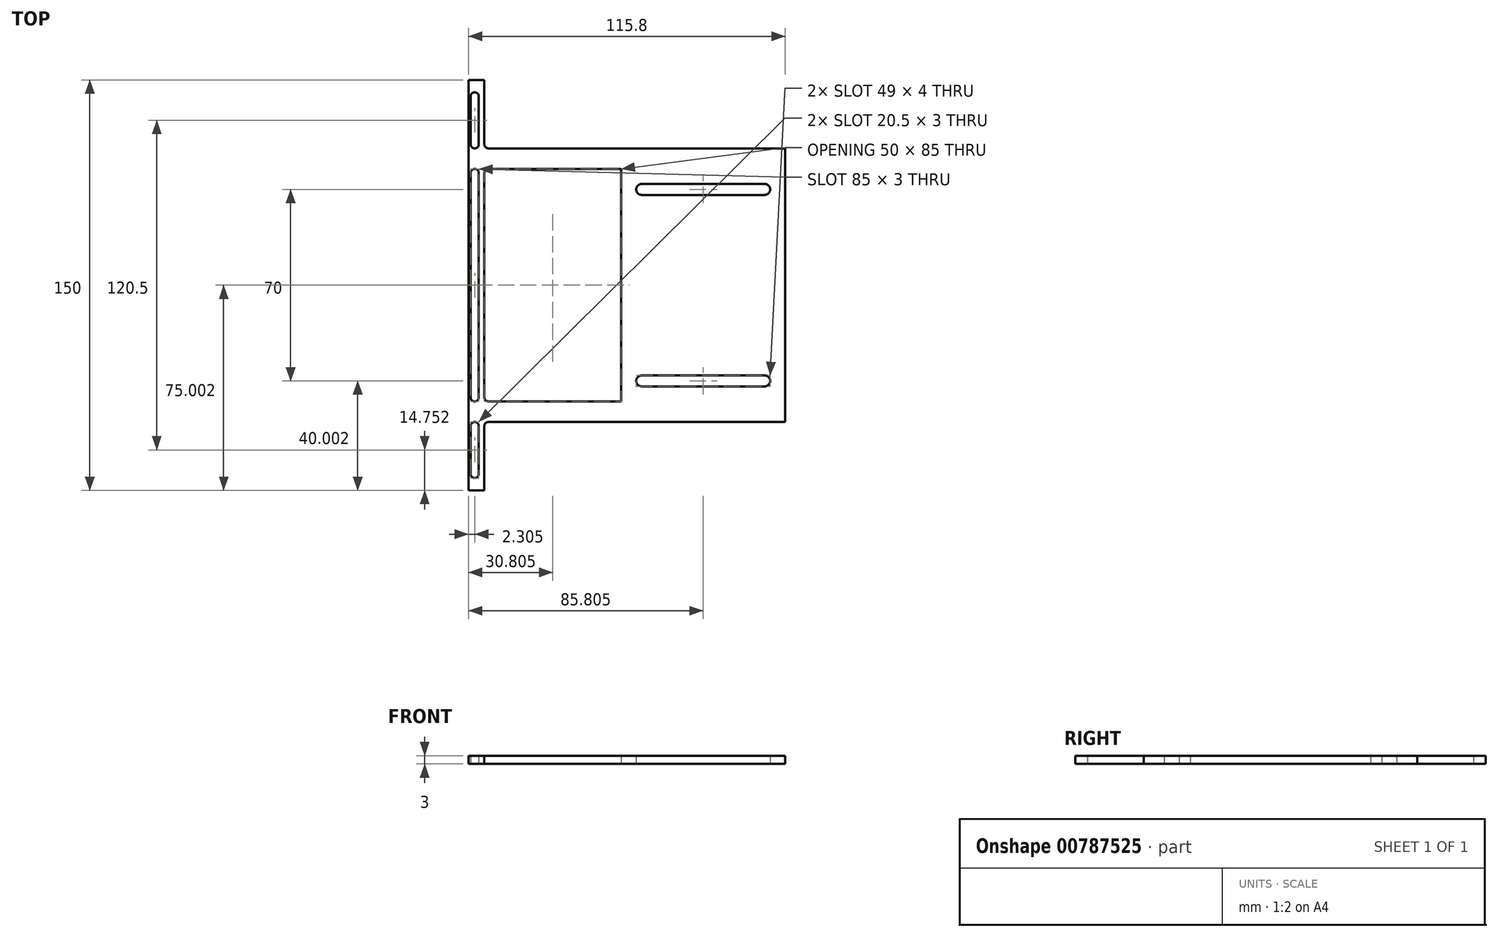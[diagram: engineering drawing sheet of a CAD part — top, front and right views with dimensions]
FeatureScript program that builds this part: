
annotation { "Feature Type Name" : "Feature", "Feature Type Description" : "" }
export const myFeature = defineFeature(function(context is Context, id is Id, definition is map)
    precondition{}
    {
        {
            var Q0;
            Q0=qCreatedBy(makeId("Top.planeOp"),FACE);
            var sketch = newSketch(context, id + "F0", { "sketchPlane" : qUnion([Q0])});
            skLineSegment(sketch, "E0.bottom", {"start": v(-8.05, 60.1) * mm, "end": v(-116.55, 60.1) * mm});
            skLineSegment(sketch, "E0.top", {"start": v(-8.05, -39.9) * mm, "end": v(-116.55, -39.9) * mm});
            skLineSegment(sketch, "E0.left", {"start": v(-8.05, 60.1) * mm, "end": v(-8.05, -39.9) * mm});
            skLineSegment(sketch, "E0.right", {"start": v(-118.05, 51.1) * mm, "end": v(-118.05, -30.9) * mm});
            skLineSegment(sketch, "E1.bottom", {"start": v(-116.55, 52.6) * mm, "end": v(-68.05, 52.6) * mm});
            skLineSegment(sketch, "E1.top", {"start": v(-116.55, -32.4) * mm, "end": v(-68.05, -32.4) * mm});
            skLineSegment(sketch, "E1.right", {"start": v(-68.05, 52.6) * mm, "end": v(-68.05, -32.4) * mm});
            skLineSegment(sketch, "E2.bottom", {"start": v(-118.05, 85.1) * mm, "end": v(-123.85, 85.1) * mm});
            skLineSegment(sketch, "E2.top", {"start": v(-118.05, -64.9) * mm, "end": v(-123.85, -64.9) * mm});
            skLineSegment(sketch, "E2.left", {"start": v(-118.05, 85.1) * mm, "end": v(-118.05, 61.6) * mm});
            skLineSegment(sketch, "E2.right", {"start": v(-123.85, 85.1) * mm, "end": v(-123.85, -64.9) * mm});
            skLineSegment(sketch, "E3.trimOffspring", {"start": v(-118.05, -41.4) * mm, "end": v(-118.05, -64.9) * mm});
            skLineSegment(sketch, "E4.trimOffspring", {"start": v(-118.05, 52.6) * mm, "end": v(-118.05, -32.4) * mm});
            skArc(sketch, "E5", {"start": v(-15.55, 43.1) * mm, "mid": v(-13.55, 45.1) * mm, "end": v(-15.55, 47.1) * mm});
            skArc(sketch, "E6", {"start": v(-60.55, 47.1) * mm, "mid": v(-62.55, 45.1) * mm, "end": v(-60.55, 43.1) * mm});
            skLineSegment(sketch, "E7", {"start": v(-60.55, 47.1) * mm, "end": v(-15.55, 47.1) * mm});
            skLineSegment(sketch, "E8", {"start": v(-60.55, 43.1) * mm, "end": v(-15.55, 43.1) * mm});
            skLineSegment(sketch, "E9", {"start": v(-8.05, 10.1) * mm, "end": v(-21.34, 10.1) * mm, "construction": true});
            skArc(sketch, "E10.MirrorCS", {"start": v(-60.55, -26.9) * mm, "mid": v(-62.55, -24.9) * mm, "end": v(-60.55, -22.9) * mm});
            skArc(sketch, "E11.MirrorCS", {"start": v(-15.55, -22.9) * mm, "mid": v(-13.55, -24.9) * mm, "end": v(-15.55, -26.9) * mm});
            skLineSegment(sketch, "E12.MirrorCS", {"start": v(-60.55, -26.9) * mm, "end": v(-15.55, -26.9) * mm});
            skLineSegment(sketch, "E13.MirrorCS", {"start": v(-60.55, -22.9) * mm, "end": v(-15.55, -22.9) * mm});
            skLineSegment(sketch, "E14.0", {"start": v(-121.55, 79.1) * mm, "end": v(-121.55, -58.9) * mm, "construction": true});
            skLineSegment(sketch, "E15.0", {"start": v(-123.05, 79.1) * mm, "end": v(-123.05, 61.6) * mm});
            skLineSegment(sketch, "E16.0", {"start": v(-120.05, 79.1) * mm, "end": v(-120.05, 61.6) * mm});
            skArc(sketch, "E17", {"start": v(-123.05, -58.9) * mm, "mid": v(-121.55, -60.4) * mm, "end": v(-120.05, -58.9) * mm});
            skArc(sketch, "E18", {"start": v(-120.05, 79.1) * mm, "mid": v(-121.55, 80.6) * mm, "end": v(-123.05, 79.1) * mm});
            skLineSegment(sketch, "E19", {"start": v(-121.55, -32.4) * mm, "end": v(-121.55, -32.4) * mm});
            skLineSegment(sketch, "E20", {"start": v(-121.55, -39.9) * mm, "end": v(-121.55, -39.9) * mm});
            skLineSegment(sketch, "E21.trimOffspring", {"start": v(-120.05, -41.4) * mm, "end": v(-120.05, -58.9) * mm});
            skLineSegment(sketch, "E22.trimOffspring", {"start": v(-123.05, -41.4) * mm, "end": v(-123.05, -58.9) * mm});
            skLineSegment(sketch, "E23", {"start": v(-121.55, 60.1) * mm, "end": v(-121.55, 60.1) * mm});
            skLineSegment(sketch, "E24", {"start": v(-121.55, 52.6) * mm, "end": v(-121.55, 52.6) * mm});
            skLineSegment(sketch, "E25.trimOffspring", {"start": v(-123.05, 51.1) * mm, "end": v(-123.05, -30.9) * mm});
            skLineSegment(sketch, "E26.trimOffspring", {"start": v(-120.05, 51.1) * mm, "end": v(-120.05, -30.9) * mm});
            skPoint(sketch, "E27.visualSharp", {"position": v(-120.05, 60.1) * mm});
            skArc(sketch, "E27.filletArc", {"start": v(-121.55, 60.1) * mm, "mid": v(-120.48, 60.54) * mm, "end": v(-120.05, 61.6) * mm});
            skPoint(sketch, "E28.visualSharp", {"position": v(-123.05, 60.1) * mm});
            skArc(sketch, "E28.filletArc", {"start": v(-123.05, 61.6) * mm, "mid": v(-122.6, 60.54) * mm, "end": v(-121.55, 60.1) * mm});
            skPoint(sketch, "E29.visualSharp", {"position": v(-123.05, 52.6) * mm});
            skArc(sketch, "E29.filletArc", {"start": v(-121.55, 52.6) * mm, "mid": v(-122.6, 52.16) * mm, "end": v(-123.05, 51.1) * mm});
            skPoint(sketch, "E30.visualSharp", {"position": v(-120.05, 52.6) * mm});
            skArc(sketch, "E30.filletArc", {"start": v(-120.05, 51.1) * mm, "mid": v(-120.48, 52.16) * mm, "end": v(-121.55, 52.6) * mm});
            skPoint(sketch, "E31.visualSharp", {"position": v(-123.05, -32.4) * mm});
            skArc(sketch, "E31.filletArc", {"start": v(-123.05, -30.9) * mm, "mid": v(-122.6, -31.96) * mm, "end": v(-121.55, -32.4) * mm});
            skPoint(sketch, "E32.visualSharp", {"position": v(-120.05, -32.4) * mm});
            skArc(sketch, "E32.filletArc", {"start": v(-121.55, -32.4) * mm, "mid": v(-120.48, -31.96) * mm, "end": v(-120.05, -30.9) * mm});
            skPoint(sketch, "E33.visualSharp", {"position": v(-123.05, -39.9) * mm});
            skArc(sketch, "E33.filletArc", {"start": v(-121.55, -39.9) * mm, "mid": v(-122.6, -40.34) * mm, "end": v(-123.05, -41.4) * mm});
            skPoint(sketch, "E34.visualSharp", {"position": v(-120.05, -39.9) * mm});
            skArc(sketch, "E34.filletArc", {"start": v(-120.05, -41.4) * mm, "mid": v(-120.48, -40.34) * mm, "end": v(-121.55, -39.9) * mm});
            skPoint(sketch, "E35.visualSharp", {"position": v(-118.05, -39.9) * mm});
            skArc(sketch, "E35.filletArc", {"start": v(-116.55, -39.9) * mm, "mid": v(-117.6, -40.34) * mm, "end": v(-118.05, -41.4) * mm});
            skPoint(sketch, "E36.visualSharp", {"position": v(-118.05, -32.4) * mm});
            skArc(sketch, "E36.filletArc", {"start": v(-118.05, -30.9) * mm, "mid": v(-117.6, -31.96) * mm, "end": v(-116.55, -32.4) * mm});
            skPoint(sketch, "E37.visualSharp", {"position": v(-118.05, 52.6) * mm});
            skArc(sketch, "E37.filletArc", {"start": v(-116.55, 52.6) * mm, "mid": v(-117.6, 52.16) * mm, "end": v(-118.05, 51.1) * mm});
            skPoint(sketch, "E38.visualSharp", {"position": v(-118.05, 60.1) * mm});
            skArc(sketch, "E38.filletArc", {"start": v(-118.05, 61.6) * mm, "mid": v(-117.6, 60.54) * mm, "end": v(-116.55, 60.1) * mm});
            skSolve(sketch);
        }
        {
            var Q0;
            Q0=makeQuery(id+"F0.imprint","IMPRINT",FACE,{"disambiguationData":[TD([[makeQuery(id+"F0.imprint","IMPRINT",EDGE,{"derivedFrom":sQuery(id+"F0.wireOp",EDGE,"E0.bottom")}),1.0]])]});
            extrude(context, id + "F1", {"entities" : qUnion([Q0]), "depth" : 3 * mm, "offsetDistance" : 25.4 * mm});
        }
    });
